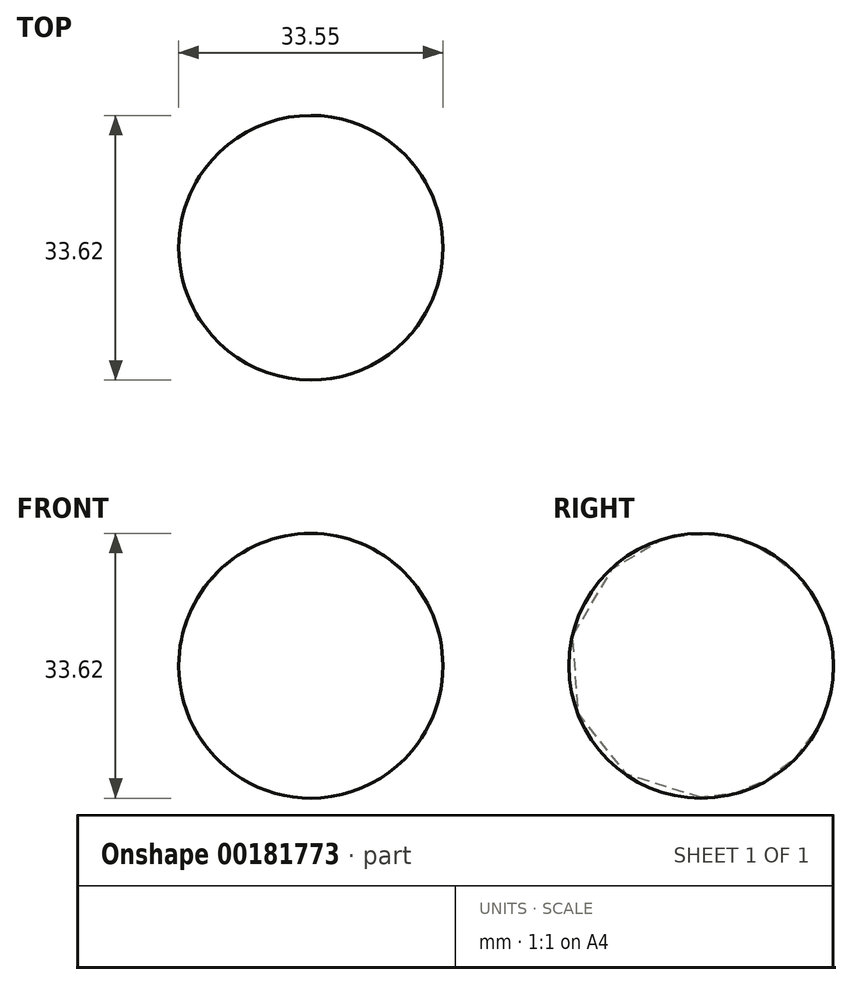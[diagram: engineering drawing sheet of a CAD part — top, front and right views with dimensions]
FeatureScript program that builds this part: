
annotation { "Feature Type Name" : "Feature", "Feature Type Description" : "" }
export const myFeature = defineFeature(function(context is Context, id is Id, definition is map)
    precondition{}
    {
        {
            var Q0;
            Q0=qCreatedBy(makeId("Front.planeOp"),FACE);
            var sketch = newSketch(context, id + "F0", { "sketchPlane" : qUnion([Q0])});
            skLineSegment(sketch, "E0", {"start": v(-16.1, 0) * mm, "end": v(17.45, 0) * mm});
            skArc(sketch, "E1", {"start": v(17.45, 0) * mm, "mid": v(0.68, 16.73) * mm, "end": v(-16.1, 0) * mm});
            skSolve(sketch);
        }
        {
            var Q0;
            Q0=makeQuery(id+"F0.imprint","IMPRINT",FACE,{"disambiguationData":[TD([[makeQuery(id+"F0.imprint","IMPRINT",EDGE,{"derivedFrom":sQuery(id+"F0.wireOp",EDGE,"E0")}),1.0]])]});
            var Q1;
            Q1=sQuery(id+"F0.wireOp",EDGE,"E0");
            revolve(context, id + "F1", {"entities" : qUnion([Q0]), "axis" : qUnion([Q1]), "revolveType" : RevolveType.FULL});
        }
    });
